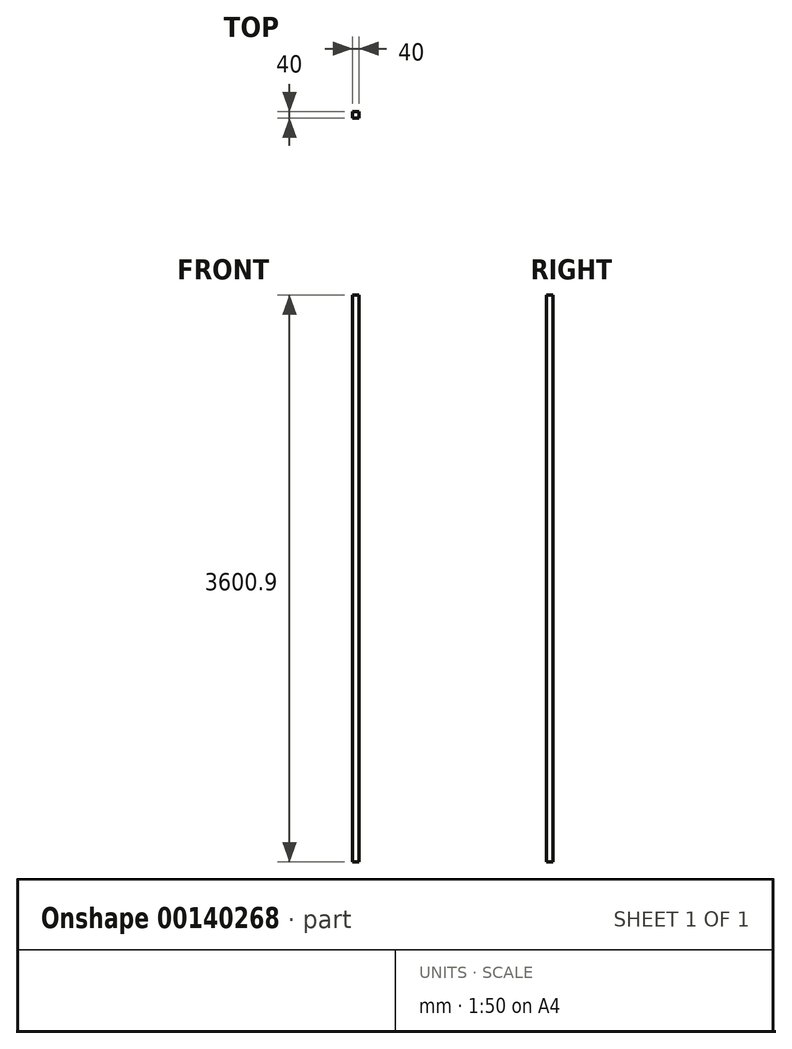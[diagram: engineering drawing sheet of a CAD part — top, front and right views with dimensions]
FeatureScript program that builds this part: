
annotation { "Feature Type Name" : "Feature", "Feature Type Description" : "" }
export const myFeature = defineFeature(function(context is Context, id is Id, definition is map)
    precondition{}
    {
        {
            var Q0;
            Q0=qCreatedBy(makeId("Top.planeOp"),FACE);
            var sketch = newSketch(context, id + "F0", { "sketchPlane" : qUnion([Q0])});
            skLineSegment(sketch, "E0.bottom", {"start": v(-20, 20) * mm, "end": v(20, 20) * mm});
            skLineSegment(sketch, "E0.top", {"start": v(-20, -20) * mm, "end": v(20, -20) * mm});
            skLineSegment(sketch, "E0.left", {"start": v(-20, 20) * mm, "end": v(-20, -20) * mm});
            skLineSegment(sketch, "E0.right", {"start": v(20, 20) * mm, "end": v(20, -20) * mm});
            skSolve(sketch);
        }
        {
            var Q0;
            Q0=makeQuery(id+"F0.imprint","IMPRINT",FACE,{"disambiguationData":[TD([[makeQuery(id+"F0.imprint","IMPRINT",EDGE,{"derivedFrom":sQuery(id+"F0.wireOp",EDGE,"E0.bottom")}),-1.0]])]});
            extrude(context, id + "F1", {"entities" : qUnion([Q0]), "depth" : 1800 * mm});
        }
        {
            var Q0;
            Q0=makeQuery(id+"F1.opExtrude","CAP_FACE",FACE,{"disambiguationData":[OSD([sQuery(id+"F0.wireOp",EDGE,"E0.bottom"),sQuery(id+"F0.wireOp",EDGE,"E0.top"),sQuery(id+"F0.wireOp",EDGE,"E0.left"),sQuery(id+"F0.wireOp",EDGE,"E0.right")])],"isStart":true});
            extrude(context, id + "F2", {"entities" : qUnion([Q0]), "operationType" : NewBodyOperationType.ADD, "endBound" : BoundingType.THROUGH_ALL, "depth" : 25 * mm});
        }
    });
